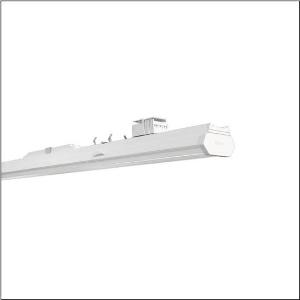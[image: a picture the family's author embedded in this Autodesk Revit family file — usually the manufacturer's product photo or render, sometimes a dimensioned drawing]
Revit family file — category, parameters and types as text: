
# Revit family: licross_r__11_protected_mo_51td12mn4axg_dbc1
name_source: partatom
category: Lighting Fixtures
units: mm (PartAtom-declared; Revit-internal decimal feet)

## family parameters
Cut with Voids When Loaded = No
Host = Face
Light Source = No
Part Type = Normal
Room Calculation Point = No
Round Connector Dimension = Use Diameter
Shared = No

## types (1)
- --- (1 x LED, 10020 lm, 55.3 W, 4000K)
    Apparent Load = 55 VA
    CIE Flux Codes = 73 92 98 99 100
    Color Rendering = 80
    Color Temperature = 4000K
    Default Elevation = 1800 mm
    Description = Licross® 11 Protected MO, luminaire insert, of sheet steel, galvanised, coil coated, white, length: 1.500mm, width: 90mm, height: 101mm, LED rated luminous flux: 10.030lm, light colour: 840, control gear: ON/OFF Multilumen, with plug, 3-pole, with phase selection, mains connection: 220..240V, AC, 50/60Hz, rated input power: 55W, halogen-free wiring, primary light control with lens, of plastic, primary optical cover: cover, of PMMA, light emission: direct distribution, primary light characteristic: symmetric, protection rating (complete): IP54, insulation class (complete): insulation class I (protective earthing), certification: CE, ENEC, VDE, UKCA, protection symbol: D if used in an environment with non-conductive dust loads with corresponding accessories, impact resistance: IK06, permissible ambient temperature for indoor applications: -35..+40°C, corresponds to IFS (International Featured Standards) requirements for safety and quality in the food industry, reducing of maximum allowable ambient temperature of 5°C with ceiling mounting, LABS conformity tested according to VDMA 24364:2018-05, packaging unit: 1 piece
    Height = 92 mm
    Lamp = 1 x LED
    Lamp Light Flux = 10020 lm
    Lamp Power = 55.3 W
    Lamp count = 1
    Length = 1500 mm
    Luminous efficacy = 181 lm/W
    Manufacturer = Siteco
    ModVariant = No
    Model = 51TD12MN4AXG
    Mounting Place = Ceiling
    Mounting Type = Pendant
    Number of Poles = 1
    OnlyDefault = Yes
    Power Factor = 1
    Product Name = Licross® 11 Protected MO
    Product group = luminaire insert
    ProductGroupID = 901
    Protection Class = Protection class I
    Protection Degree = IP 54
    RLX_Detail_Level = 1
    RLX_Emergency_Light_Flux = 0 lm
    RLX_Emergency_Type = 0
    RLX_Emergency_Type_DB = No
    RlxData = <blob elided: 22173 chars, md5=e142c92e>
    Socket = socket
    Standby Power = 0 W
    System Light Flux = 10020 lm
    System Power = 55 W
    Type Comments = factory setting: luminous flux: 100 % | (A | C | E) | 126 mA
    Type Image = l_1256145.jpg
    URL = http://relux.com
    VarID = @adj_019447
    Voltage = 0 V
    Weight = 0.00 kg
    Width = 88 mm

## geometry (parser evidence)
native form markers: Blend x4, Sweep x12
no freeform markers — native parametric forms only
